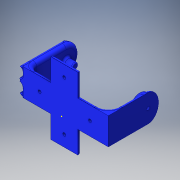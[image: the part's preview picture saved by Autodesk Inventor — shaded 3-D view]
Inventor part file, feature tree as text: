
AUTODESK INVENTOR PART (.ipt)
format: ipt  version: 2016 (Build 200138000, 138)  size: 600,576 bytes
history: native  units: in
note: dims shown in document units (in); Inventor stores cm internally (conversion verified against a paired STEP export)
features: extrude x12, sketch x12, fillet x12, hole x2
ambient origin geometry x8: Origin, YZ Plane, XZ Plane, XY Plane, X Axis, Y Axis, Z Axis, Center Point
bodies: Solid1 (feature_tree)
feature tree (38):
  extrude  "Extrusion1"  Depth=0.5197in
  extrude  "Extrusion3"  Depth=0.0787in
  sketch  "Sketch5"  dims[d9=0.9449in d10=0.0in d11=0.2835in]
  extrude  "Extrusion4"  Depth=0.2835in
  extrude  "Extrusion5"  Depth=0.2598in
  fillet  "Fillet1"  Radius=0.2598in
  fillet  "Fillet4"  Radius=0.5197in
  fillet  "Fillet5"  Radius=0.3622in
  fillet  "Fillet6"  Radius=0.1437in
  fillet  "Fillet7"  Radius=0.2224in
  extrude  "Extrusion6"  Depth=0.0787in
  sketch  "Sketch9"  dims[d24=0.0787in d25=0.0in d27=0.0787in]
  extrude  "Extrusion7"  Depth=0.0197in
  fillet  "Fillet10"  Radius=0.0197in
  fillet  "Fillet11"  Radius=0.0394in
  sketch  "Sketch10"  dims[d28=0.0787in d29=0.0in d30=0.1969in d33=0.0197in d34=0.0394in]
  extrude  "Extrusion8"  Depth=0.0197in
  extrude  "Extrusion10"  Depth=0.9449in TaperAngle=0.0deg
  extrude  "Extrusion11"  Depth=0.2598in
  sketch  "Sketch17"  dims[d43=0.2598in d44=0.2598in]
  hole  "Hole2"  [1 undecoded]
  fillet  "Fillet18"  Radius=0.1772in
  extrude  "Extrusion12"  Depth=0.0197in
  extrude  "Extrusion13"  Depth=0.0197in TaperAngle=0.0deg
  fillet  "Fillet22"  Radius=0.5197in
  hole  "Hole3"  [1 undecoded]
  extrude  "Extrusion15"  Depth=0.0197in
  fillet  "Fillet24"  Radius=0.4291in
  fillet  "Fillet25"  Radius=0.5866in
  fillet  "Fillet26"  Radius=0.4291in
  sketch  "Sketch1"  dims[d0=1.6535in d1=0.5197in]
  sketch  "Sketch4"  dims[d2=0.0787in d3=0.0in d8=0.0787in]
  sketch  "Sketch7"  dims[d12=0.2598in d13=0.2598in d14=0.2598in d15=0.5197in d16=0.3622in d17=0.1437in d19=0.2224in]
  sketch  "Sketch15"  dims[d35=0.0394in d36=0.0197in]
  sketch  "Sketch16"  dims[d37=0.0787in d38=0.9449in d39=0.0in]
  sketch  "Sketch18"  dims[d45=0.2598in d46=0.1181in d47=0.1772in d48=0.0in]
  sketch  "Sketch19"  dims[d49=0.0394in d50=0.0197in]
  sketch  "Sketch20"  dims[d51=0.1181in d52=0.1181in d53=0.0in d82=0.5197in d83=0.5472in d84=0.5866in d85=0.4291in d86=0.0in d87=0.5866in d88=0.4291in d89=0.0in d90=0.0591in d91=0.2362in d92=0.1575in d93=0.0787in d94=90.0deg d95=0.315in d96=0.8108in d98=0.1181in d99=0.5591in d100=0.5591in d101=0.5591in d103=0.4291in d104=0.0in d106=0.0591in d107=0.4291in d108=0.0in d111=0.0748in d112=0.0591in d113=0.2362in d114=0.1575in d115=0.0787in d116=90.0deg d117=0.315in d118=0.8108in d124=0.0591in d125=0.0591in d126=0.0in d127=0.0787in d128=0.0197in d129=0.0197in]
note: 2 required parameter values undecoded (feature->parameter linkage not recoverable at this tier; creation-order binding heuristic only, values carry confidence <= 0.55)
